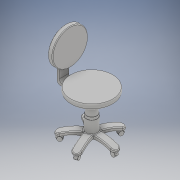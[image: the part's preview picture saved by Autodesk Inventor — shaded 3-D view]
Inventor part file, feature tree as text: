
AUTODESK INVENTOR PART (.ipt)
format: ipt  version: 2017 (Build 210142000, 142)  size: 727,552 bytes
history: native  units: in
note: dims shown in document units (in); Inventor stores cm internally (conversion verified against a paired STEP export)
features: sketch x16, extrude x14, fillet x8, other x4, plane x1, mirror x1, pattern_circular x1
ambient origin geometry x8: Origin, YZ Plane, XZ Plane, XY Plane, X Axis, Y Axis, Z Axis, Center Point
bodies: Solid1 (feature_tree)
feature tree (45):
  extrude  "seat"  Depth=1.1875in
  fillet  "curve bottom of seat"  Radius=0.625in
  fillet  "curv top of seat"  Radius=0.3in
  extrude  "solenoid connection to seat"  [1 undecoded]
  fillet  "curve solenoid connection to seat"  Radius=4.5in
  plane  "Work Plane1"
  extrude  "solnoid connection to back rest horizantal"  Depth=0.5in
  extrude  "solnoid connection to back rest vertical"  Depth=1.417in
  fillet  "curve back rest connection outer"  Radius=0.25in
  fillet  "curve back rest connection inner"  Radius=0.1in
  sketch  "Sketch6"  dims[d18=0.7in d19=0.0in d20=0.1in d21=0.342in]
  extrude  "connection to back rest extextion"  Depth=0.1in
  fillet  "curve connection to back rest extextion"  Radius=0.342in
  extrude  "back rest"  Depth=0.406in
  fillet  "smooth back rest"  Radius=1.6845in
  other  "solnoid"
  extrude  "foot of chair"  Depth=0.3867in
  extrude  "curve added to foot"  Depth=1.7843in
  extrude  "smooth out the end of the foot"  Depth=1.161in
  extrude  "wheel connection to foot"  Depth=1.0in TaperAngle=0.0deg
  extrude  "wheel case"  Depth=0.6667in
  extrude  "wheel protection make"  Depth=3.0in TaperAngle=0.0deg
  extrude  "wheel protection cut"  Depth=0.0927in TaperAngle=0.0deg
  extrude  "wheel"  Depth=0.3438in TaperAngle=0.0deg
  other  "wheel curve face workplane"
  other  "wheel for foot"
  mirror  "Mirror the components for the wheel"
  pattern_circular  "Circular the foot"  [2 undecoded]
  fillet  "smooth out the feet"  Radius=0.7057in
  sketch  "Sketch1"  dims[d0=1.2in d1=0.0in d2=1.1875in d3=0.625in d4=0.3in d5=0.0in]
  sketch  "Sketch2"  dims[d6=0.5in d7=-0.5in d8=4.5in d9=0.0in]
  sketch  "Sketch4"  dims[d10=5.5in d11=0.0in d12=0.5in]
  sketch  "Sketch5"  dims[d13=0.5in d14=1.417in d15=0.25in d16=0.0in d17=0.1in]
  sketch  "Sketch8"  dims[d22=0.246in d23=0.406in d24=1.6845in]
  sketch  "Sketch9"  dims[d25=0.0417in d26=0.3867in]
  sketch  "Sketch10"  dims[d27=0.0417in d28=1.7843in]
  sketch  "Sketch11"  dims[d29=90.0deg d34=1.161in]
  sketch  "Sketch12"  dims[d35=3.1875in d36=1.0in d37=0.0in]
  sketch  "Sketch13"  dims[d38=0.3333in d39=0.6667in]
  sketch  "Sketch15"  dims[d40=0.6667in d41=3.0in d42=0.0in]
  sketch  "Sketch16"  dims[d43=0.1955in d44=0.0927in d45=0.0in]
  sketch  "Sketch17"  dims[d46=0.4947in d47=0.3438in d48=0.0in]
  other  "Work Axis1"
  sketch  "Sketch19"  dims[d50=0.3855in]
  sketch  "Sketch21"  dims[d52=0.7247in d53=0.5in d54=0.0in d55=0.7057in d56=0.1585in d57=0.0in d58=0.648in d59=0.2283in d60=0.0in d63=90.0deg d71=0.2095in d72=0.0in d83=1.9685in d84=360.0deg d86=0.125in]
note: 3 required parameter values undecoded (feature->parameter linkage not recoverable at this tier; creation-order binding heuristic only, values carry confidence <= 0.55)
